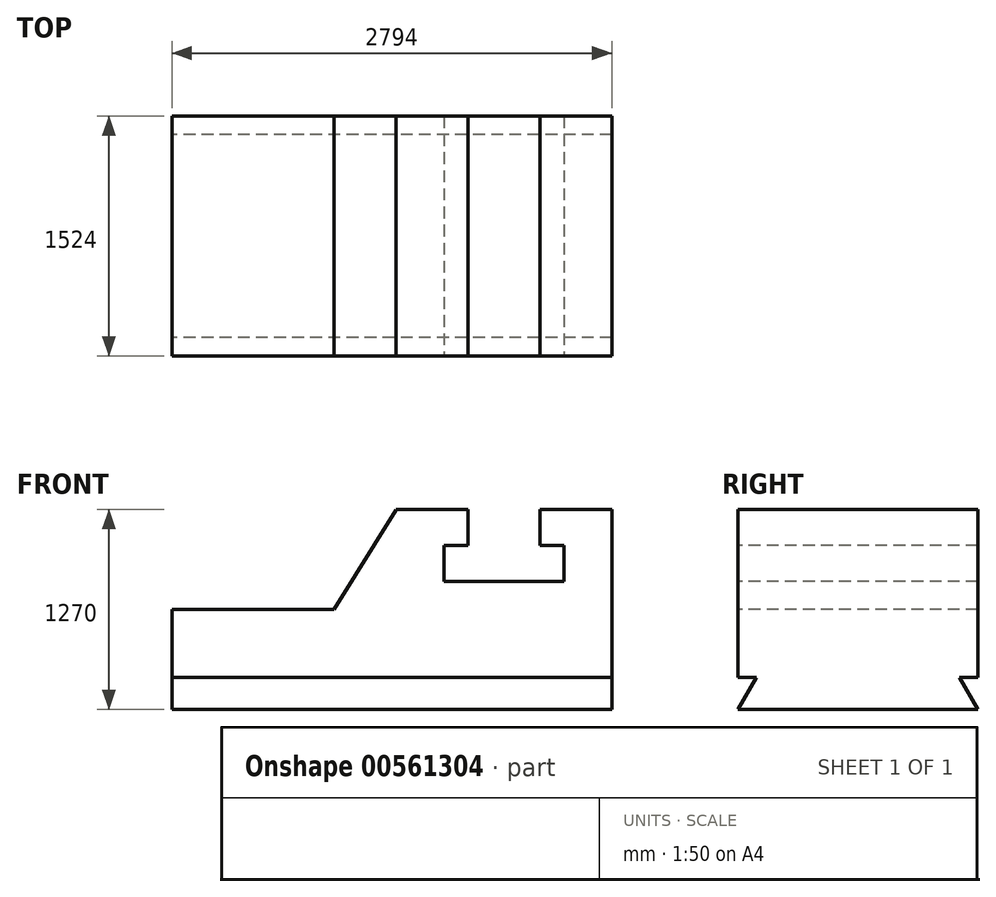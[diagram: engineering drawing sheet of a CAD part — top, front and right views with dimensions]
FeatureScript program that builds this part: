
annotation { "Feature Type Name" : "Feature", "Feature Type Description" : "" }
export const myFeature = defineFeature(function(context is Context, id is Id, definition is map)
    precondition{}
    {
        {
            var Q0;
            Q0=qCreatedBy(makeId("Top.planeOp"),FACE);
            var sketch = newSketch(context, id + "F0", { "sketchPlane" : qUnion([Q0])});
            skLineSegment(sketch, "E0.bottom", {"start": v(-1422.4, 904.24) * mm, "end": v(1371.6, 904.24) * mm});
            skLineSegment(sketch, "E0.top", {"start": v(-1422.4, -619.76) * mm, "end": v(1371.6, -619.76) * mm});
            skLineSegment(sketch, "E0.left", {"start": v(-1422.4, 904.24) * mm, "end": v(-1422.4, -619.76) * mm});
            skLineSegment(sketch, "E0.right", {"start": v(1371.6, 904.24) * mm, "end": v(1371.6, -619.76) * mm});
            skLineSegment(sketch, "E1", {"start": v(1371.6, 904.24) * mm, "end": v(914.4, 904.24) * mm});
            skLineSegment(sketch, "E2", {"start": v(914.4, 904.24) * mm, "end": v(914.4, -619.76) * mm});
            skLineSegment(sketch, "E3", {"start": v(914.4, -619.76) * mm, "end": v(1371.6, -619.76) * mm});
            skLineSegment(sketch, "E4", {"start": v(914.4, 904.24) * mm, "end": v(457.2, 904.24) * mm});
            skLineSegment(sketch, "E5", {"start": v(457.2, 904.24) * mm, "end": v(457.2, -619.76) * mm});
            skLineSegment(sketch, "E6", {"start": v(457.2, -619.76) * mm, "end": v(914.4, -619.76) * mm});
            skLineSegment(sketch, "E7", {"start": v(457.2, -619.76) * mm, "end": v(0, -619.76) * mm});
            skLineSegment(sketch, "E8", {"start": v(0, -619.76) * mm, "end": v(0, 904.24) * mm});
            skLineSegment(sketch, "E9", {"start": v(0, 904.24) * mm, "end": v(457.2, 904.24) * mm});
            skLineSegment(sketch, "E10", {"start": v(-392.08, 904.24) * mm, "end": v(-392.08, -619.76) * mm});
            skSolve(sketch);
        }
        {
            var Q0;
            {var subQ0=sQuery(id+"F0.wireOp",EDGE,"E0.left");Q0=makeQuery(id+"F0.imprint","IMPRINT",FACE,{"disambiguationData":[TD([[makeQuery(id+"F0.imprint","IMPRINT",EDGE,{"derivedFrom":subQ0}),1.0]])]});}
            extrude(context, id + "F1", {"entities" : qUnion([Q0]), "depth" : 635 * mm, "offsetDistance" : 25.4 * mm});
        }
        {
            var Q0;
            Q0=makeQuery(id+"F0.imprint","IMPRINT",FACE,{"disambiguationData":[TD([[makeQuery(id+"F0.imprint","IMPRINT",EDGE,{"derivedFrom":sQuery(id+"F0.wireOp",EDGE,"E5")}),-1.0]])]});
            var Q1;
            Q1=makeQuery(id+"F0.imprint","IMPRINT",FACE,{"disambiguationData":[TD([[makeQuery(id+"F0.imprint","IMPRINT",EDGE,{"derivedFrom":sQuery(id+"F0.wireOp",EDGE,"E2")}),-1.0]])]});
            var Q2;
            Q2=makeQuery(id+"F0.imprint","IMPRINT",FACE,{"disambiguationData":[TD([[makeQuery(id+"F0.imprint","IMPRINT",EDGE,{"derivedFrom":sQuery(id+"F0.wireOp",EDGE,"E0.right")}),-1.0]])]});
            extrude(context, id + "F2", {"entities" : qUnion([Q0, Q1, Q2]), "depth" : 1270 * mm, "offsetDistance" : 25.4 * mm});
        }
        {
            var Q0;
            {var subQ0=sQuery(id+"F0.wireOp",EDGE,"E8");Q0=makeQuery(id+"F0.imprint","IMPRINT",FACE,{"disambiguationData":[TD([[makeQuery(id+"F0.imprint","IMPRINT",EDGE,{"derivedFrom":subQ0}),1.0]])]});}
            extrude(context, id + "F3", {"entities" : qUnion([Q0]), "depth" : 635 * mm, "offsetDistance" : 25.4 * mm});
        }
        {
            var Q0;
            Q0=makeQuery(id+"F3.opExtrude","SWEPT_FACE",FACE,{"disambiguationData":[OSD([sQuery(id+"F0.wireOp",EDGE,"E0.top")])]});
            var sketch = newSketch(context, id + "F4", { "sketchPlane" : qUnion([Q0])});
            skLineSegment(sketch, "E11", {"start": v(-392.08, 635) * mm, "end": v(0, 635) * mm});
            skLineSegment(sketch, "E12", {"start": v(0, 635) * mm, "end": v(0, 1266.98) * mm});
            skLineSegment(sketch, "E13", {"start": v(0, 1266.98) * mm, "end": v(-392.08, 635) * mm});
            skSolve(sketch);
        }
        {
            var Q0;
            Q0 = qSketchRegion(id + "F4", true);
            extrude(context, id + "F5", {"entities" : qUnion([Q0]), "oppositeDirection" : true, "depth" : 1524 * mm, "offsetDistance" : 25.4 * mm});
        }
        {
            var Q0;
            Q0=makeQuery(id+"F1.opExtrude","SWEPT_FACE",FACE,{"disambiguationData":[OSD([sQuery(id+"F0.wireOp",EDGE,"E0.left")])]});
            var sketch = newSketch(context, id + "F6", { "sketchPlane" : qUnion([Q0])});
            skLineSegment(sketch, "E14", {"start": v(-904.24, 0) * mm, "end": v(-904.24, 203.2) * mm});
            skLineSegment(sketch, "E15", {"start": v(-904.24, 203.2) * mm, "end": v(-786.92, 203.2) * mm});
            skLineSegment(sketch, "E16", {"start": v(-786.92, 203.2) * mm, "end": v(-904.24, 0) * mm});
            skLineSegment(sketch, "E17", {"start": v(619.76, 0) * mm, "end": v(619.76, 203.2) * mm});
            skLineSegment(sketch, "E18", {"start": v(619.76, 203.2) * mm, "end": v(502.44, 203.2) * mm});
            skLineSegment(sketch, "E19", {"start": v(502.44, 203.2) * mm, "end": v(619.76, 0) * mm});
            skSolve(sketch);
        }
        {
            var Q0;
            Q0=makeQuery(id+"F2.opExtrude","SWEPT_BODY",BODY,{"disambiguationData":[OSD([sQuery(id+"F0.wireOp",EDGE,"E0.right"),sQuery(id+"F0.wireOp",EDGE,"E1"),sQuery(id+"F0.wireOp",EDGE,"E3"),sQuery(id+"F0.wireOp",EDGE,"E4"),sQuery(id+"F0.wireOp",EDGE,"E6"),sQuery(id+"F0.wireOp",EDGE,"E7"),sQuery(id+"F0.wireOp",EDGE,"E8"),sQuery(id+"F0.wireOp",EDGE,"E9")])]});
            var Q1;
            Q1=makeQuery(id+"F5.opExtrude","SWEPT_BODY",BODY,{"disambiguationData":[OSD([sQuery(id+"F4.wireOp",EDGE,"E11"),sQuery(id+"F4.wireOp",EDGE,"E12"),sQuery(id+"F4.wireOp",EDGE,"E13")])]});
            var Q2;
            Q2=makeQuery(id+"F3.opExtrude","SWEPT_BODY",BODY,{"disambiguationData":[OSD([sQuery(id+"F0.wireOp",EDGE,"E0.bottom"),sQuery(id+"F0.wireOp",EDGE,"E0.top"),sQuery(id+"F0.wireOp",EDGE,"E8"),sQuery(id+"F0.wireOp",EDGE,"E10")])]});
            var Q3;
            Q3=makeQuery(id+"F1.opExtrude","SWEPT_BODY",BODY,{"disambiguationData":[OSD([sQuery(id+"F0.wireOp",EDGE,"E0.bottom"),sQuery(id+"F0.wireOp",EDGE,"E0.top"),sQuery(id+"F0.wireOp",EDGE,"E0.left"),sQuery(id+"F0.wireOp",EDGE,"E10")])]});
            booleanBodies(context, id + "F7", {"operationType" : BooleanOperationType.UNION, "tools" : qUnion([Q0, Q1, Q2, Q3])});
        }
        {
            var Q0;
            Q0=makeQuery(id+"F6.imprint","IMPRINT",FACE,{"disambiguationData":[TD([[makeQuery(id+"F6.imprint","IMPRINT",EDGE,{"derivedFrom":sQuery(id+"F6.wireOp",EDGE,"E17")}),-1.0]])]});
            extrude(context, id + "F8", {"entities" : qUnion([Q0]), "operationType" : NewBodyOperationType.REMOVE, "endBound" : BoundingType.THROUGH_ALL, "oppositeDirection" : true, "depth" : 25.4 * mm, "offsetDistance" : 25.4 * mm});
        }
        {
            var Q0;
            Q0=makeQuery(id+"F6.imprint","IMPRINT",FACE,{"disambiguationData":[TD([[makeQuery(id+"F6.imprint","IMPRINT",EDGE,{"derivedFrom":sQuery(id+"F6.wireOp",EDGE,"E14")}),1.0]])]});
            extrude(context, id + "F9", {"entities" : qUnion([Q0]), "operationType" : NewBodyOperationType.REMOVE, "endBound" : BoundingType.THROUGH_ALL, "oppositeDirection" : true, "depth" : 25.4 * mm, "offsetDistance" : 25.4 * mm});
        }
        {
            var Q0;
            {var subQ0=sQuery(id+"F0.wireOp",EDGE,"E0.top");Q0=makeQuery(id+"F7.opBoolean","MERGE",FACE,{"derivedFrom":[makeQuery(id+"F1.opExtrude","SWEPT_FACE",FACE,{"disambiguationData":[OSD([subQ0])]}),makeQuery(id+"F2.opExtrude","SWEPT_FACE",FACE,{"disambiguationData":[OSD([sQuery(id+"F0.wireOp",EDGE,"E3"),sQuery(id+"F0.wireOp",EDGE,"E6"),sQuery(id+"F0.wireOp",EDGE,"E7")])]}),makeQuery(id+"F3.opExtrude","SWEPT_FACE",FACE,{"disambiguationData":[OSD([subQ0])]}),makeQuery(id+"F5.opExtrude","CAP_FACE",FACE,{"disambiguationData":[OSD([sQuery(id+"F4.wireOp",EDGE,"E11"),sQuery(id+"F4.wireOp",EDGE,"E12"),sQuery(id+"F4.wireOp",EDGE,"E13")])],"isStart":true})]});}
            var sketch = newSketch(context, id + "F10", { "sketchPlane" : qUnion([Q0])});
            skLineSegment(sketch, "E20", {"start": v(1371.6, 1270) * mm, "end": v(914.4, 1270) * mm});
            skLineSegment(sketch, "E21", {"start": v(914.4, 1270) * mm, "end": v(914.4, 1041.4) * mm});
            skLineSegment(sketch, "E22", {"start": v(0, 1270) * mm, "end": v(457.2, 1270) * mm});
            skLineSegment(sketch, "E23", {"start": v(457.2, 1270) * mm, "end": v(457.2, 1041.4) * mm});
            skLineSegment(sketch, "E24", {"start": v(457.2, 1041.4) * mm, "end": v(304.8, 1041.4) * mm});
            skLineSegment(sketch, "E25", {"start": v(914.4, 1041.4) * mm, "end": v(1066.8, 1041.4) * mm});
            skLineSegment(sketch, "E26", {"start": v(304.8, 1041.4) * mm, "end": v(304.8, 812.8) * mm});
            skLineSegment(sketch, "E27", {"start": v(1066.8, 1041.4) * mm, "end": v(1066.8, 812.8) * mm});
            skLineSegment(sketch, "E28", {"start": v(304.8, 812.8) * mm, "end": v(1066.8, 812.8) * mm});
            skLineSegment(sketch, "E29", {"start": v(457.2, 1270) * mm, "end": v(914.4, 1270) * mm});
            skSolve(sketch);
        }
        {
            var Q0;
            Q0=makeQuery(id+"F10.imprint","IMPRINT",FACE,{"disambiguationData":[TD([[makeQuery(id+"F10.imprint","IMPRINT",EDGE,{"derivedFrom":sQuery(id+"F10.wireOp",EDGE,"E21")}),-1.0]])]});
            extrude(context, id + "F11", {"entities" : qUnion([Q0]), "operationType" : NewBodyOperationType.REMOVE, "endBound" : BoundingType.THROUGH_ALL, "oppositeDirection" : true, "depth" : 25.4 * mm, "offsetDistance" : 25.4 * mm});
        }
    });
